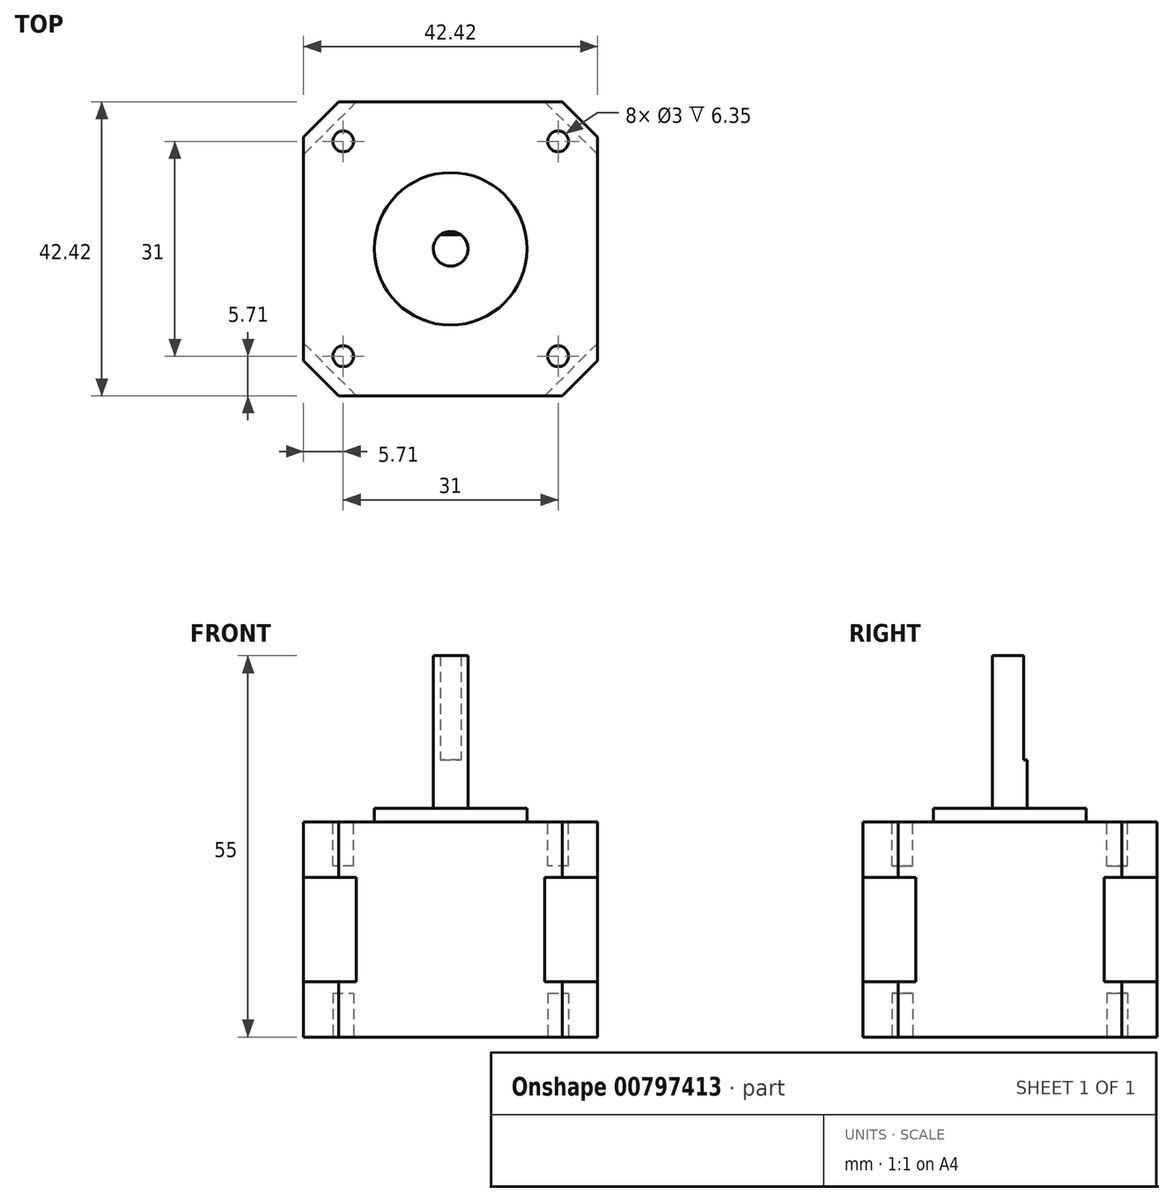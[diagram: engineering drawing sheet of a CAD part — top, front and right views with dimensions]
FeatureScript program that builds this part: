
annotation { "Feature Type Name" : "Feature", "Feature Type Description" : "" }
export const myFeature = defineFeature(function(context is Context, id is Id, definition is map)
    precondition{}
    {
        {
            var Q0;
            Q0=qCreatedBy(makeId("Top.planeOp"),FACE);
            var sketch = newSketch(context, id + "F0", { "sketchPlane" : qUnion([Q0])});
            skLineSegment(sketch, "E0.bottom", {"start": v(-21.2, 21.2) * mm, "end": v(21.2, 21.2) * mm});
            skLineSegment(sketch, "E0.top", {"start": v(-21.2, -21.2) * mm, "end": v(21.2, -21.2) * mm});
            skLineSegment(sketch, "E0.left", {"start": v(-21.2, 21.2) * mm, "end": v(-21.2, -21.2) * mm});
            skLineSegment(sketch, "E0.right", {"start": v(21.2, 21.2) * mm, "end": v(21.2, -21.2) * mm});
            skSolve(sketch);
        }
        {
            assignVariable(context, id + "F1", {"name" : "Steppertussen", "anyValue" : 15});
        }
        {
            assignVariable(context, id + "F2", {"name" : "Stepperrand", "anyValue" : 8});
        }
        {
            assignVariable(context, id + "F3", {"name" : "Stepperashoogte", "anyValue" : 22});
        }
        {
            var Q0;
            Q0=makeQuery(id+"F0.imprint","IMPRINT",FACE,{"disambiguationData":[TD([[makeQuery(id+"F0.imprint","IMPRINT",EDGE,{"derivedFrom":sQuery(id+"F0.wireOp",EDGE,"E0.bottom")}),-1.0]])]});
            extrude(context, id + "F4", {"entities" : qUnion([Q0]), "endBound" : BoundingType.SYMMETRIC, "depth" : (getVariable(context, 'Steppertussen')) * mm, "offsetDistance" : 25 * mm});
        }
        {
            var Q0;
            Q0=makeQuery(id+"F4.opExtrude","SWEPT_EDGE",EDGE,{"disambiguationData":[OSD([sQuery(id+"F0.wireOp",EDGE,"E0.bottom"),sQuery(id+"F0.wireOp",EDGE,"E0.right")])]});
            var Q1;
            Q1=makeQuery(id+"F4.opExtrude","SWEPT_EDGE",EDGE,{"disambiguationData":[OSD([sQuery(id+"F0.wireOp",EDGE,"E0.bottom"),sQuery(id+"F0.wireOp",EDGE,"E0.left")])]});
            var Q2;
            Q2=makeQuery(id+"F4.opExtrude","SWEPT_EDGE",EDGE,{"disambiguationData":[OSD([sQuery(id+"F0.wireOp",EDGE,"E0.top"),sQuery(id+"F0.wireOp",EDGE,"E0.left")])]});
            var Q3;
            Q3=makeQuery(id+"F4.opExtrude","SWEPT_EDGE",EDGE,{"disambiguationData":[OSD([sQuery(id+"F0.wireOp",EDGE,"E0.top"),sQuery(id+"F0.wireOp",EDGE,"E0.right")])]});
            chamfer(context, id + "F5", {"entities" : qUnion([Q0, Q1, Q2, Q3]), "width" : 7.62 * mm, "tangentPropagation" : true});
        }
        {
            var Q0;
            Q0=makeQuery(id+"F4.opExtrude","CAP_FACE",FACE,{"disambiguationData":[OSD([sQuery(id+"F0.wireOp",EDGE,"E0.bottom"),sQuery(id+"F0.wireOp",EDGE,"E0.top"),sQuery(id+"F0.wireOp",EDGE,"E0.left"),sQuery(id+"F0.wireOp",EDGE,"E0.right")])],"isStart":false});
            var sketch = newSketch(context, id + "F6", { "sketchPlane" : qUnion([Q0])});
            skLineSegment(sketch, "E1.bottom", {"start": v(-21.2, 21.2) * mm, "end": v(21.2, 21.2) * mm});
            skLineSegment(sketch, "E1.top", {"start": v(-21.2, -21.2) * mm, "end": v(21.2, -21.2) * mm});
            skLineSegment(sketch, "E1.left", {"start": v(-21.2, 21.2) * mm, "end": v(-21.2, -21.2) * mm});
            skLineSegment(sketch, "E1.right", {"start": v(21.2, 21.2) * mm, "end": v(21.2, -21.2) * mm});
            skSolve(sketch);
        }
        {
            var Q0;
            {var subQ0=sQuery(id+"F0.wireOp",EDGE,"E0.top");var subQ1=sQuery(id+"F0.wireOp",EDGE,"E0.right");var subQ2=sQuery(id+"F0.wireOp",EDGE,"E0.bottom");var subQ3=sQuery(id+"F0.wireOp",EDGE,"E0.left");var subQ4=makeQuery(id+"F4.opExtrude","CAP_FACE",FACE,{"disambiguationData":[OSD([subQ2,subQ0,subQ3,subQ1])],"isStart":false});var subQ8=makeQuery(id+"F5.opChamfer","BLEND_EDGE",EDGE,{"blendedFrom":[makeQuery(id+"F4.opExtrude","SWEPT_EDGE",EDGE,{"disambiguationData":[OSD([subQ2,subQ3])]}),subQ4],"blendedInto":[subQ4]});Q0=makeQuery(id+"F6.imprint","IMPRINT",FACE,{"disambiguationData":[TD([[makeQuery(id+"F6.imprint","IMPRINT",EDGE,{"derivedFrom":subQ8}),1.0]])]});}
            var Q1;
            {var subQ0=sQuery(id+"F0.wireOp",EDGE,"E0.bottom");var subQ1=sQuery(id+"F0.wireOp",EDGE,"E0.right");var subQ2=makeQuery(id+"F5.opChamfer","BLEND_EDGE",EDGE,{"blendedFrom":[makeQuery(id+"F4.opExtrude","SWEPT_EDGE",EDGE,{"disambiguationData":[OSD([subQ0,subQ1])]}),makeQuery(id+"F4.opExtrude","CAP_FACE",FACE,{"disambiguationData":[OSD([subQ0,sQuery(id+"F0.wireOp",EDGE,"E0.top"),sQuery(id+"F0.wireOp",EDGE,"E0.left"),subQ1])],"isStart":false})],"blendedInto":[makeQuery(id+"F4.opExtrude","CAP_FACE",FACE,{"disambiguationData":[OSD([subQ0,sQuery(id+"F0.wireOp",EDGE,"E0.top"),sQuery(id+"F0.wireOp",EDGE,"E0.left"),subQ1])],"isStart":false})]});Q1=makeQuery(id+"F6.imprint","IMPRINT",FACE,{"disambiguationData":[TD([[makeQuery(id+"F6.imprint","IMPRINT",EDGE,{"derivedFrom":subQ2}),-1.0]])]});}
            var Q2;
            {var subQ0=sQuery(id+"F0.wireOp",EDGE,"E0.bottom");var subQ1=sQuery(id+"F0.wireOp",EDGE,"E0.left");var subQ2=makeQuery(id+"F5.opChamfer","BLEND_EDGE",EDGE,{"blendedFrom":[makeQuery(id+"F4.opExtrude","SWEPT_EDGE",EDGE,{"disambiguationData":[OSD([subQ0,subQ1])]}),makeQuery(id+"F4.opExtrude","CAP_FACE",FACE,{"disambiguationData":[OSD([subQ0,sQuery(id+"F0.wireOp",EDGE,"E0.top"),subQ1,sQuery(id+"F0.wireOp",EDGE,"E0.right")])],"isStart":false})],"blendedInto":[makeQuery(id+"F4.opExtrude","CAP_FACE",FACE,{"disambiguationData":[OSD([subQ0,sQuery(id+"F0.wireOp",EDGE,"E0.top"),subQ1,sQuery(id+"F0.wireOp",EDGE,"E0.right")])],"isStart":false})]});Q2=makeQuery(id+"F6.imprint","IMPRINT",FACE,{"disambiguationData":[TD([[makeQuery(id+"F6.imprint","IMPRINT",EDGE,{"derivedFrom":subQ2}),-1.0]])]});}
            var Q3;
            {var subQ0=sQuery(id+"F0.wireOp",EDGE,"E0.top");var subQ1=sQuery(id+"F0.wireOp",EDGE,"E0.left");var subQ2=makeQuery(id+"F5.opChamfer","BLEND_EDGE",EDGE,{"blendedFrom":[makeQuery(id+"F4.opExtrude","SWEPT_EDGE",EDGE,{"disambiguationData":[OSD([subQ0,subQ1])]}),makeQuery(id+"F4.opExtrude","CAP_FACE",FACE,{"disambiguationData":[OSD([sQuery(id+"F0.wireOp",EDGE,"E0.bottom"),subQ0,subQ1,sQuery(id+"F0.wireOp",EDGE,"E0.right")])],"isStart":false})],"blendedInto":[makeQuery(id+"F4.opExtrude","CAP_FACE",FACE,{"disambiguationData":[OSD([sQuery(id+"F0.wireOp",EDGE,"E0.bottom"),subQ0,subQ1,sQuery(id+"F0.wireOp",EDGE,"E0.right")])],"isStart":false})]});Q3=makeQuery(id+"F6.imprint","IMPRINT",FACE,{"disambiguationData":[TD([[makeQuery(id+"F6.imprint","IMPRINT",EDGE,{"derivedFrom":subQ2}),-1.0]])]});}
            var Q4;
            {var subQ0=sQuery(id+"F0.wireOp",EDGE,"E0.top");var subQ1=sQuery(id+"F0.wireOp",EDGE,"E0.right");var subQ2=makeQuery(id+"F5.opChamfer","BLEND_EDGE",EDGE,{"blendedFrom":[makeQuery(id+"F4.opExtrude","SWEPT_EDGE",EDGE,{"disambiguationData":[OSD([subQ0,subQ1])]}),makeQuery(id+"F4.opExtrude","CAP_FACE",FACE,{"disambiguationData":[OSD([sQuery(id+"F0.wireOp",EDGE,"E0.bottom"),subQ0,sQuery(id+"F0.wireOp",EDGE,"E0.left"),subQ1])],"isStart":false})],"blendedInto":[makeQuery(id+"F4.opExtrude","CAP_FACE",FACE,{"disambiguationData":[OSD([sQuery(id+"F0.wireOp",EDGE,"E0.bottom"),subQ0,sQuery(id+"F0.wireOp",EDGE,"E0.left"),subQ1])],"isStart":false})]});Q4=makeQuery(id+"F6.imprint","IMPRINT",FACE,{"disambiguationData":[TD([[makeQuery(id+"F6.imprint","IMPRINT",EDGE,{"derivedFrom":subQ2}),-1.0]])]});}
            extrude(context, id + "F7", {"entities" : qUnion([Q0, Q1, Q2, Q3, Q4]), "operationType" : NewBodyOperationType.ADD, "depth" : (getVariable(context, 'Stepperrand')) * mm, "offsetDistance" : 25 * mm});
        }
        {
            var Q0;
            Q0=makeQuery(id+"F7.opExtrude","SWEPT_EDGE",EDGE,{"disambiguationData":[OSD([sQuery(id+"F6.wireOp",EDGE,"E1.bottom"),sQuery(id+"F6.wireOp",EDGE,"E1.right")])]});
            var Q1;
            Q1=makeQuery(id+"F7.opExtrude","SWEPT_EDGE",EDGE,{"disambiguationData":[OSD([sQuery(id+"F6.wireOp",EDGE,"E1.bottom"),sQuery(id+"F6.wireOp",EDGE,"E1.left")])]});
            var Q2;
            Q2=makeQuery(id+"F7.opExtrude","SWEPT_EDGE",EDGE,{"disambiguationData":[OSD([sQuery(id+"F6.wireOp",EDGE,"E1.top"),sQuery(id+"F6.wireOp",EDGE,"E1.left")])]});
            var Q3;
            Q3=makeQuery(id+"F7.opExtrude","SWEPT_EDGE",EDGE,{"disambiguationData":[OSD([sQuery(id+"F6.wireOp",EDGE,"E1.top"),sQuery(id+"F6.wireOp",EDGE,"E1.right")])]});
            chamfer(context, id + "F8", {"entities" : qUnion([Q0, Q1, Q2, Q3]), "width" : 5.08 * mm, "tangentPropagation" : true});
        }
        {
            var Q0;
            Q0=makeQuery(id+"F4.opExtrude","CAP_FACE",FACE,{"disambiguationData":[OSD([sQuery(id+"F0.wireOp",EDGE,"E0.bottom"),sQuery(id+"F0.wireOp",EDGE,"E0.top"),sQuery(id+"F0.wireOp",EDGE,"E0.left"),sQuery(id+"F0.wireOp",EDGE,"E0.right")])],"isStart":true});
            var sketch = newSketch(context, id + "F9", { "sketchPlane" : qUnion([Q0])});
            skLineSegment(sketch, "E2.0.0", {"start": v(-16.13, 21.2) * mm, "end": v(16.13, 21.2) * mm});
            skLineSegment(sketch, "E2.0.1", {"start": v(16.13, 21.2) * mm, "end": v(21.2, 16.13) * mm});
            skLineSegment(sketch, "E2.0.2", {"start": v(21.2, -16.13) * mm, "end": v(21.2, 16.13) * mm});
            skLineSegment(sketch, "E2.0.3", {"start": v(21.2, -16.13) * mm, "end": v(16.13, -21.2) * mm});
            skLineSegment(sketch, "E2.0.4", {"start": v(-16.13, -21.2) * mm, "end": v(16.13, -21.2) * mm});
            skLineSegment(sketch, "E2.0.5", {"start": v(-16.13, -21.2) * mm, "end": v(-21.2, -16.13) * mm});
            skLineSegment(sketch, "E2.0.6", {"start": v(-21.2, -16.13) * mm, "end": v(-21.2, 16.13) * mm});
            skLineSegment(sketch, "E2.0.7", {"start": v(-21.2, 16.13) * mm, "end": v(-16.13, 21.2) * mm});
            skSolve(sketch);
        }
        {
            var Q0;
            {var subQ3=sQuery(id+"F9.wireOp",EDGE,"E2.0.7");Q0=makeQuery(id+"F9.imprint","IMPRINT",FACE,{"disambiguationData":[TD([[makeQuery(id+"F9.imprint","IMPRINT",EDGE,{"derivedFrom":subQ3}),-1.0]])]});}
            var Q1;
            {var subQ4=sQuery(id+"F9.wireOp",EDGE,"E2.0.1");Q1=makeQuery(id+"F9.imprint","IMPRINT",FACE,{"disambiguationData":[TD([[makeQuery(id+"F9.imprint","IMPRINT",EDGE,{"derivedFrom":subQ4}),-1.0]])]});}
            var Q2;
            {var subQ4=sQuery(id+"F9.wireOp",EDGE,"E2.0.3");Q2=makeQuery(id+"F9.imprint","IMPRINT",FACE,{"disambiguationData":[TD([[makeQuery(id+"F9.imprint","IMPRINT",EDGE,{"derivedFrom":subQ4}),-1.0]])]});}
            var Q3;
            {var subQ4=sQuery(id+"F9.wireOp",EDGE,"E2.0.5");Q3=makeQuery(id+"F9.imprint","IMPRINT",FACE,{"disambiguationData":[TD([[makeQuery(id+"F9.imprint","IMPRINT",EDGE,{"derivedFrom":subQ4}),-1.0]])]});}
            var Q4;
            {var subQ0=sQuery(id+"F0.wireOp",EDGE,"E0.top");var subQ1=sQuery(id+"F0.wireOp",EDGE,"E0.right");var subQ2=sQuery(id+"F0.wireOp",EDGE,"E0.bottom");var subQ3=sQuery(id+"F0.wireOp",EDGE,"E0.left");var subQ4=makeQuery(id+"F4.opExtrude","CAP_FACE",FACE,{"disambiguationData":[OSD([subQ2,subQ0,subQ3,subQ1])],"isStart":true});var subQ8=makeQuery(id+"F5.opChamfer","BLEND_EDGE",EDGE,{"blendedFrom":[makeQuery(id+"F4.opExtrude","SWEPT_EDGE",EDGE,{"disambiguationData":[OSD([subQ2,subQ3])]}),subQ4],"blendedInto":[subQ4]});Q4=makeQuery(id+"F9.imprint","IMPRINT",FACE,{"disambiguationData":[TD([[makeQuery(id+"F9.imprint","IMPRINT",EDGE,{"derivedFrom":subQ8}),1.0]])]});}
            extrude(context, id + "F10", {"entities" : qUnion([Q0, Q1, Q2, Q3, Q4]), "operationType" : NewBodyOperationType.ADD, "depth" : (getVariable(context, 'Stepperrand')) * mm, "offsetDistance" : 25 * mm});
        }
        {
            var Q0;
            Q0=makeQuery(id+"F7.opExtrude","CAP_FACE",FACE,{"disambiguationData":[OSD([sQuery(id+"F6.wireOp",EDGE,"E1.bottom"),sQuery(id+"F6.wireOp",EDGE,"E1.top"),sQuery(id+"F6.wireOp",EDGE,"E1.left"),sQuery(id+"F6.wireOp",EDGE,"E1.right")])],"isStart":false});
            var sketch = newSketch(context, id + "F11", { "sketchPlane" : qUnion([Q0])});
            skCircle(sketch, "E3", {"center": v(0, 0) * mm, "radius": 11 * mm});
            skSolve(sketch);
        }
        {
            var Q0;
            Q0=makeQuery(id+"F11.imprint","IMPRINT",FACE,{"disambiguationData":[TD([[makeQuery(id+"F11.imprint","IMPRINT",EDGE,{"derivedFrom":sQuery(id+"F11.wireOp",EDGE,"E3")}),1.0]])]});
            extrude(context, id + "F12", {"entities" : qUnion([Q0]), "operationType" : NewBodyOperationType.ADD, "depth" : 2 * mm});
        }
        {
            var Q0;
            Q0=makeQuery(id+"F12.opExtrude","CAP_FACE",FACE,{"disambiguationData":[OSD([sQuery(id+"F11.wireOp",EDGE,"E3")])],"isStart":false});
            var sketch = newSketch(context, id + "F13", { "sketchPlane" : qUnion([Q0])});
            skCircle(sketch, "E4", {"center": v(0, 0) * mm, "radius": 2.5 * mm});
            skSolve(sketch);
        }
        {
            var Q0;
            Q0=makeQuery(id+"F13.imprint","IMPRINT",FACE,{"disambiguationData":[TD([[makeQuery(id+"F13.imprint","IMPRINT",EDGE,{"derivedFrom":sQuery(id+"F13.wireOp",EDGE,"E4")}),1.0]])]});
            extrude(context, id + "F14", {"entities" : qUnion([Q0]), "operationType" : NewBodyOperationType.ADD, "depth" : (getVariable(context, 'Stepperashoogte')) * mm, "offsetDistance" : 25 * mm});
        }
        {
            var Q0;
            Q0=makeQuery(id+"F14.opExtrude","CAP_FACE",FACE,{"disambiguationData":[OSD([sQuery(id+"F13.wireOp",EDGE,"E4")])],"isStart":false});
            var sketch = newSketch(context, id + "F15", { "sketchPlane" : qUnion([Q0])});
            skLineSegment(sketch, "E5.bottom", {"start": v(-2.63, 2.93) * mm, "end": v(2.62, 2.93) * mm});
            skLineSegment(sketch, "E5.top", {"start": v(-2.63, 2) * mm, "end": v(2.62, 2) * mm});
            skLineSegment(sketch, "E5.left", {"start": v(-2.63, 2.93) * mm, "end": v(-2.63, 2) * mm});
            skLineSegment(sketch, "E5.right", {"start": v(2.62, 2.93) * mm, "end": v(2.62, 2) * mm});
            skSolve(sketch);
        }
        {
            var Q0;
            {var subQ0=makeQuery(id+"F14.opExtrude","CAP_EDGE",EDGE,{"disambiguationData":[OSD([sQuery(id+"F13.wireOp",EDGE,"E4")])],"isStart":false});var subQ1=sQuery(id+"F15.wireOp",EDGE,"E5.top");var subQ3=makeQuery(id+"F15.imprint","INTERSECT",VERTEX,{"disambiguationData":[OD(0.0)],"derivedFrom":[subQ0,subQ1]});Q0=qUnion([makeQuery(id+"F15.imprint","IMPRINT",FACE,{"disambiguationData":[TD([[makeQuery(id+"F15.imprint","IMPRINT",EDGE,{"derivedFrom":sQuery(id+"F15.wireOp",EDGE,"E5.bottom")}),-1.0]])]}),makeQuery(id+"F15.imprint","IMPRINT",FACE,{"disambiguationData":[TD([[makeQuery(id+"F15.imprint","IMPRINT",EDGE,{"disambiguationData":[TD([[subQ3,-1.0]])],"derivedFrom":subQ1}),1.0]])]})]);}
            extrude(context, id + "F16", {"entities" : qUnion([Q0]), "operationType" : NewBodyOperationType.REMOVE, "oppositeDirection" : true, "depth" : 15 * mm});
        }
        {
            var Q0;
            Q0=makeQuery(id+"F7.opExtrude","CAP_FACE",FACE,{"disambiguationData":[OSD([sQuery(id+"F6.wireOp",EDGE,"E1.bottom"),sQuery(id+"F6.wireOp",EDGE,"E1.top"),sQuery(id+"F6.wireOp",EDGE,"E1.left"),sQuery(id+"F6.wireOp",EDGE,"E1.right")])],"isStart":false});
            var sketch = newSketch(context, id + "F17", { "sketchPlane" : qUnion([Q0])});
            skCircle(sketch, "E6", {"center": v(-15.5, 15.5) * mm, "radius": 1.5 * mm});
            skCircle(sketch, "E7", {"center": v(15.5, 15.5) * mm, "radius": 1.5 * mm});
            skCircle(sketch, "E8", {"center": v(15.5, -15.5) * mm, "radius": 1.5 * mm});
            skCircle(sketch, "E9", {"center": v(-15.5, -15.5) * mm, "radius": 1.5 * mm});
            skLineSegment(sketch, "E10", {"start": v(-45.53, 0) * mm, "end": v(50.04, 0) * mm, "construction": true});
            skLineSegment(sketch, "E11", {"start": v(0, -35.63) * mm, "end": v(0, 35.98) * mm, "construction": true});
            skLineSegment(sketch, "E12.rect.bottom", {"start": v(-15.5, 15.5) * mm, "end": v(15.5, 15.5) * mm, "construction": true});
            skLineSegment(sketch, "E12.rect.top", {"start": v(-15.5, -15.5) * mm, "end": v(15.5, -15.5) * mm, "construction": true});
            skLineSegment(sketch, "E12.rect.left", {"start": v(-15.5, 15.5) * mm, "end": v(-15.5, -15.5) * mm, "construction": true});
            skLineSegment(sketch, "E12.rect.right", {"start": v(15.5, 15.5) * mm, "end": v(15.5, -15.5) * mm, "construction": true});
            skPoint(sketch, "E12.rect.middle", {"position": v(0, 0) * mm});
            skPoint(sketch, "E13", {"position": v(0, 15.5) * mm});
            skSolve(sketch);
        }
        {
            var Q0;
            {Q0=qUnion([makeQuery(id+"F17.imprint","IMPRINT",FACE,{"disambiguationData":[TD([[makeQuery(id+"F17.imprint","IMPRINT",EDGE,{"derivedFrom":sQuery(id+"F17.wireOp",EDGE,"E6")}),1.0]])]}),makeQuery(id+"F17.imprint","IMPRINT",FACE,{"disambiguationData":[TD([[makeQuery(id+"F17.imprint","IMPRINT",EDGE,{"derivedFrom":sQuery(id+"F17.wireOp",EDGE,"E7")}),1.0]])]}),makeQuery(id+"F17.imprint","IMPRINT",FACE,{"disambiguationData":[TD([[makeQuery(id+"F17.imprint","IMPRINT",EDGE,{"derivedFrom":sQuery(id+"F17.wireOp",EDGE,"E8")}),1.0]])]}),makeQuery(id+"F17.imprint","IMPRINT",FACE,{"disambiguationData":[TD([[makeQuery(id+"F17.imprint","IMPRINT",EDGE,{"derivedFrom":sQuery(id+"F17.wireOp",EDGE,"E9")}),1.0]])]})]);}
            extrude(context, id + "F18", {"entities" : qUnion([Q0]), "operationType" : NewBodyOperationType.REMOVE, "oppositeDirection" : true, "depth" : 6.35 * mm});
        }
        {
            var Q0;
            Q0=makeQuery(id+"F4.opExtrude","SWEPT_BODY",BODY,{"disambiguationData":[OSD([sQuery(id+"F0.wireOp",EDGE,"E0.bottom"),sQuery(id+"F0.wireOp",EDGE,"E0.top"),sQuery(id+"F0.wireOp",EDGE,"E0.left"),sQuery(id+"F0.wireOp",EDGE,"E0.right")])]});
            transform(context, id + "F19", {"entities" : qUnion([Q0]), "transformType" : TransformType.TRANSLATION_3D, "dx" : 0 * mm, "dy" : 0 * mm, "dz" : 0 * mm, "makeCopy" : true});
        }
        {
            var Q0;
            Q0=makeQuery(id+"F19.opPattern","COPY",BODY,{"derivedFrom":makeQuery(id+"F4.opExtrude","SWEPT_BODY",BODY,{"disambiguationData":[OSD([sQuery(id+"F0.wireOp",EDGE,"E0.bottom"),sQuery(id+"F0.wireOp",EDGE,"E0.top"),sQuery(id+"F0.wireOp",EDGE,"E0.left"),sQuery(id+"F0.wireOp",EDGE,"E0.right")])]}),"instanceName":"1"});
            deleteBodies(context, id + "F20", {"entities" : qUnion([Q0])});
        }
        {
            var Q0;
            Q0=makeQuery(id+"F10.opExtrude","CAP_FACE",FACE,{"disambiguationData":[OSD([sQuery(id+"F9.wireOp",EDGE,"E2.0.0"),sQuery(id+"F9.wireOp",EDGE,"E2.0.1"),sQuery(id+"F9.wireOp",EDGE,"E2.0.2"),sQuery(id+"F9.wireOp",EDGE,"E2.0.3"),sQuery(id+"F9.wireOp",EDGE,"E2.0.4"),sQuery(id+"F9.wireOp",EDGE,"E2.0.5"),sQuery(id+"F9.wireOp",EDGE,"E2.0.6"),sQuery(id+"F9.wireOp",EDGE,"E2.0.7")])],"isStart":false});
            var sketch = newSketch(context, id + "F21", { "sketchPlane" : qUnion([Q0])});
            skCircle(sketch, "E14", {"center": v(-15.5, 15.5) * mm, "radius": 1.5 * mm});
            skCircle(sketch, "E15", {"center": v(15.5, 15.5) * mm, "radius": 1.5 * mm});
            skCircle(sketch, "E16", {"center": v(15.5, -15.5) * mm, "radius": 1.5 * mm});
            skCircle(sketch, "E17", {"center": v(-15.5, -15.5) * mm, "radius": 1.5 * mm});
            skLineSegment(sketch, "E18", {"start": v(-45.72, -1.3) * mm, "end": v(49.85, -1.3) * mm, "construction": true});
            skLineSegment(sketch, "E19", {"start": v(0, -35.63) * mm, "end": v(0, 35.98) * mm, "construction": true});
            skLineSegment(sketch, "E20.rect.bottom", {"start": v(-15.5, 15.5) * mm, "end": v(15.5, 15.5) * mm, "construction": true});
            skLineSegment(sketch, "E20.rect.top", {"start": v(-15.5, -15.5) * mm, "end": v(15.5, -15.5) * mm, "construction": true});
            skLineSegment(sketch, "E20.rect.left", {"start": v(-15.5, 15.5) * mm, "end": v(-15.5, -15.5) * mm, "construction": true});
            skLineSegment(sketch, "E20.rect.right", {"start": v(15.5, 15.5) * mm, "end": v(15.5, -15.5) * mm, "construction": true});
            skPoint(sketch, "E20.rect.middle", {"position": v(0, 0) * mm});
            skPoint(sketch, "E21", {"position": v(0, 15.5) * mm});
            skSolve(sketch);
        }
        {
            var Q0;
            Q0 = qSketchRegion(id + "F21", true);
            extrude(context, id + "F22", {"entities" : qUnion([Q0]), "operationType" : NewBodyOperationType.REMOVE, "oppositeDirection" : true, "depth" : 6.35 * mm, "offsetDistance" : 25 * mm});
        }
    });
